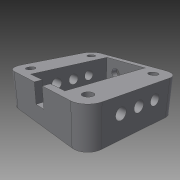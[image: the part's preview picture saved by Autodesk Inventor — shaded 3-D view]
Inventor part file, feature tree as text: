
AUTODESK INVENTOR PART (.ipt)
format: ipt  version: 2014 (Build 180170000, 170)  size: 208,384 bytes
history: native  units: mm
features: extrude x6, sketch x6, hole x1, fillet x1
ambient origin geometry x8: Origin, YZ Plane, XZ Plane, XY Plane, X Axis, Y Axis, Z Axis, Center Point
bodies: Solid1 (feature_tree)
feature tree (14):
  extrude  "Extrusion1"  Depth=37.0mm
  extrude  "Extrusion2"  Depth=3.0mm
  extrude  "Extrusion3"  Depth=37.0mm
  hole  "Hole1"  [1 undecoded]
  extrude  "Extrusion5"  Depth=8.0mm TaperAngle=0.0deg
  extrude  "Extrusion6"  Depth=6.0mm
  fillet  "Fillet2"  Radius=4.5mm
  extrude  "Extrusion7"  Depth=8.0mm
  sketch  "Sketch1"  dims[d2=21.0mm d3=37.0mm]
  sketch  "Sketch2"  dims[d11=13.0mm d12=3.0mm]
  sketch  "Sketch4"  dims[d13=3.0mm d14=0.0mm d15=37.0mm]
  sketch  "Sketch5"  dims[d16=21.0mm d17=12.0mm d18=0.0mm]
  sketch  "Sketch8"  dims[d19=5.0mm d20=8.0mm d21=0.0mm]
  sketch  "Sketch9"  dims[d22=6.5mm d23=6.5mm d24=4.0mm d25=6.0mm d26=4.0mm d27=2.0mm d28=90.0deg d29=8.0mm d30=20.594885mm d42=4.5mm d43=8.0mm d44=8.0mm d45=8.0mm d46=0.0mm d47=4.5mm d48=4.5mm d49=5.0mm d50=5.0mm d51=8.0mm d52=0.0mm d53=6.0mm d54=15.0mm d55=9.0mm d56=15.0mm d57=9.0mm d58=7.0mm d59=6.0mm d60=0.0mm]
note: 1 required parameter value undecoded (feature->parameter linkage not recoverable at this tier; creation-order binding heuristic only, values carry confidence <= 0.55)
